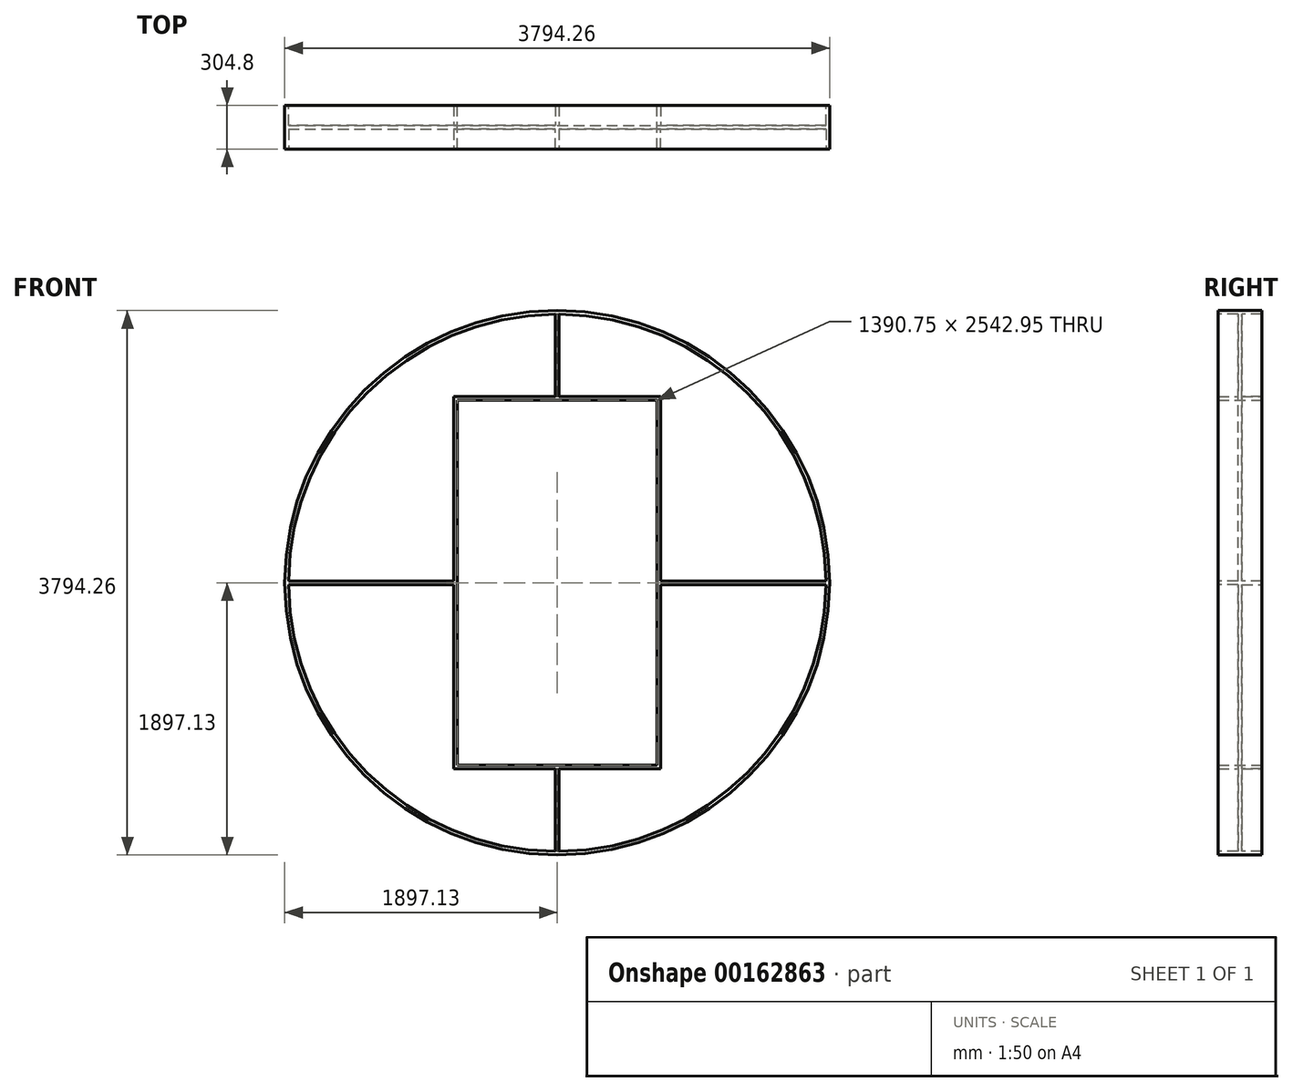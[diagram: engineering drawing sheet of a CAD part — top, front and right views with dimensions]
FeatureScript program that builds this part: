
annotation { "Feature Type Name" : "Feature", "Feature Type Description" : "" }
export const myFeature = defineFeature(function(context is Context, id is Id, definition is map)
    precondition{}
    {
        {
            var Q0;
            Q0=qCreatedBy(makeId("Front.planeOp"),FACE);
            var sketch = newSketch(context, id + "F0", { "sketchPlane" : qUnion([Q0])});
            skCircle(sketch, "E0", {"center": v(0, 0) * mm, "radius": 1897.13 * mm});
            skLineSegment(sketch, "E1.bottom", {"start": v(695.38, -1271.47) * mm, "end": v(-695.38, -1271.47) * mm});
            skLineSegment(sketch, "E1.top", {"start": v(695.38, 1271.47) * mm, "end": v(-695.38, 1271.47) * mm});
            skLineSegment(sketch, "E1.left", {"start": v(695.38, -1271.47) * mm, "end": v(695.38, 1271.47) * mm});
            skLineSegment(sketch, "E1.right", {"start": v(-695.38, -1271.47) * mm, "end": v(-695.38, 1271.47) * mm});
            skPoint(sketch, "E2.orphan", {"position": v(0, 1897.13) * mm});
            skSolve(sketch);
        }
        {
            var Q0;
            Q0 = qSketchRegion(id + "F0", true);
            extrude(context, id + "F1", {"entities" : qUnion([Q0]), "depth" : 304.8 * mm});
        }
        {
            var Q0;
            Q0=makeQuery(id+"F1.opExtrude","CAP_FACE",FACE,{"disambiguationData":[OSD([sQuery(id+"F0.wireOp",EDGE,"E0"),sQuery(id+"F0.wireOp",EDGE,"E1.bottom"),sQuery(id+"F0.wireOp",EDGE,"E1.top"),sQuery(id+"F0.wireOp",EDGE,"E1.left"),sQuery(id+"F0.wireOp",EDGE,"E1.right")])],"isStart":false});
            var sketch = newSketch(context, id + "F2", { "sketchPlane" : qUnion([Q0])});
            skCircle(sketch, "E3", {"center": v(0, 0) * mm, "radius": 1871.73 * mm});
            skLineSegment(sketch, "E4.bottom", {"start": v(720.78, -1296.87) * mm, "end": v(-720.78, -1296.87) * mm});
            skLineSegment(sketch, "E4.top", {"start": v(720.78, 1296.87) * mm, "end": v(-720.78, 1296.87) * mm});
            skLineSegment(sketch, "E4.left", {"start": v(720.78, -1296.87) * mm, "end": v(720.78, 1296.87) * mm});
            skLineSegment(sketch, "E4.right", {"start": v(-720.78, -1296.87) * mm, "end": v(-720.78, 1296.87) * mm});
            skSolve(sketch);
        }
        {
            var Q0;
            Q0 = qSketchRegion(id + "F2", true);
            extrude(context, id + "F3", {"entities" : qUnion([Q0]), "operationType" : NewBodyOperationType.REMOVE, "oppositeDirection" : true, "depth" : 139.7 * mm});
        }
        {
            var Q0;
            Q0=makeQuery(id+"F1.opExtrude","CAP_FACE",FACE,{"disambiguationData":[OSD([sQuery(id+"F0.wireOp",EDGE,"E0"),sQuery(id+"F0.wireOp",EDGE,"E1.bottom"),sQuery(id+"F0.wireOp",EDGE,"E1.top"),sQuery(id+"F0.wireOp",EDGE,"E1.left"),sQuery(id+"F0.wireOp",EDGE,"E1.right")])],"isStart":true});
            var sketch = newSketch(context, id + "F4", { "sketchPlane" : qUnion([Q0])});
            skCircle(sketch, "E5", {"center": v(0, 0) * mm, "radius": 1871.73 * mm});
            skLineSegment(sketch, "E6.bottom", {"start": v(720.78, -1296.87) * mm, "end": v(-720.78, -1296.87) * mm});
            skLineSegment(sketch, "E6.top", {"start": v(720.78, 1296.87) * mm, "end": v(-720.78, 1296.87) * mm});
            skLineSegment(sketch, "E6.left", {"start": v(720.78, -1296.87) * mm, "end": v(720.78, 1296.87) * mm});
            skLineSegment(sketch, "E6.right", {"start": v(-720.78, -1296.87) * mm, "end": v(-720.78, 1296.87) * mm});
            skSolve(sketch);
        }
        {
            var Q0;
            Q0 = qSketchRegion(id + "F4", true);
            extrude(context, id + "F5", {"entities" : qUnion([Q0]), "operationType" : NewBodyOperationType.REMOVE, "oppositeDirection" : true, "depth" : 139.7 * mm});
        }
        {
            var Q0;
            Q0=makeQuery(id+"F3.boolean.opBoolean","COPY",FACE,{"derivedFrom":makeQuery(id+"F3.opExtrude","SWEPT_FACE",FACE,{"disambiguationData":[OSD([sQuery(id+"F2.wireOp",EDGE,"E4.left")])]})});
            var sketch = newSketch(context, id + "F6", { "sketchPlane" : qUnion([Q0])});
            skLineSegment(sketch, "E7.bottom", {"start": v(-304.8, 12.7) * mm, "end": v(-165.1, 12.7) * mm});
            skLineSegment(sketch, "E7.top", {"start": v(-304.8, -12.7) * mm, "end": v(-165.1, -12.7) * mm});
            skLineSegment(sketch, "E7.left", {"start": v(-304.8, 12.7) * mm, "end": v(-304.8, -12.7) * mm});
            skPoint(sketch, "E7.middle", {"position": v(-165.1, 0) * mm});
            skLineSegment(sketch, "E8", {"start": v(-165.1, -12.7) * mm, "end": v(-165.1, 12.7) * mm});
            skPoint(sketch, "E7.right.end.orphan", {"position": v(-25.4, -12.7) * mm});
            skPoint(sketch, "E7.right.start.orphan", {"position": v(-25.4, 12.7) * mm});
            skSolve(sketch);
        }
        {
            var Q0;
            Q0 = qSketchRegion(id + "F6", true);
            var Q1;
            Q1=makeQuery(id+"F3.boolean.opBoolean","COPY",FACE,{"derivedFrom":makeQuery(id+"F3.opExtrude","SWEPT_FACE",FACE,{"disambiguationData":[OSD([sQuery(id+"F2.wireOp",EDGE,"E3")])]})});
            extrude(context, id + "F7", {"entities" : qUnion([Q0]), "endBound" : BoundingType.UP_TO_SURFACE, "endBoundEntityFace" : qUnion([Q1]), "depth" : 25.4 * mm});
        }
        {
            var Q0;
            Q0=makeQuery(id+"F7.opExtrude","SWEPT_BODY",BODY,{"disambiguationData":[OSD([sQuery(id+"F6.wireOp",EDGE,"E7.bottom"),sQuery(id+"F6.wireOp",EDGE,"E7.top"),sQuery(id+"F6.wireOp",EDGE,"E7.left"),sQuery(id+"F6.wireOp",EDGE,"E8")])]});
            var Q1;
            Q1=qCreatedBy(makeId("Right.planeOp"),FACE);
            mirror(context, id + "F8", {"operationType" : NewBodyOperationType.ADD, "entities" : qUnion([Q0]), "mirrorPlane" : qUnion([Q1])});
        }
        {
            var Q0;
            Q0=makeQuery(id+"F3.boolean.opBoolean","COPY",FACE,{"derivedFrom":makeQuery(id+"F3.opExtrude","SWEPT_FACE",FACE,{"disambiguationData":[OSD([sQuery(id+"F2.wireOp",EDGE,"E4.top")])]})});
            var sketch = newSketch(context, id + "F9", { "sketchPlane" : qUnion([Q0])});
            skLineSegment(sketch, "E9.bottom", {"start": v(-12.7, -304.8) * mm, "end": v(12.7, -304.8) * mm});
            skLineSegment(sketch, "E9.left", {"start": v(-12.7, -304.8) * mm, "end": v(-12.7, -165.1) * mm});
            skLineSegment(sketch, "E9.right", {"start": v(12.7, -304.8) * mm, "end": v(12.7, -165.1) * mm});
            skPoint(sketch, "E9.middle", {"position": v(0, -165.1) * mm});
            skLineSegment(sketch, "E10", {"start": v(12.7, -165.1) * mm, "end": v(-12.7, -165.1) * mm});
            skPoint(sketch, "E9.top.end.orphan", {"position": v(12.7, -25.4) * mm});
            skPoint(sketch, "E9.top.start.orphan", {"position": v(-12.7, -25.4) * mm});
            skSolve(sketch);
        }
        {
            var Q0;
            Q0 = qSketchRegion(id + "F9", true);
            var Q1;
            {var subQ1=sQuery(id+"F2.wireOp",EDGE,"E3");var subQ2=makeQuery(id+"F7.opExtrude","SWEPT_FACE",FACE,{"disambiguationData":[OSD([sQuery(id+"F6.wireOp",EDGE,"E7.bottom")])]});Q1=makeQuery(id+"F8.boolean.opBoolean","SPLIT",FACE,{"disambiguationData":[TD([subQ2])],"derivedFrom":makeQuery(id+"F3.boolean.opBoolean","COPY",FACE,{"derivedFrom":makeQuery(id+"F3.opExtrude","SWEPT_FACE",FACE,{"disambiguationData":[OSD([subQ1])]})})});}
            extrude(context, id + "F10", {"entities" : qUnion([Q0]), "endBound" : BoundingType.UP_TO_SURFACE, "endBoundEntityFace" : qUnion([Q1]), "depth" : 25.4 * mm});
        }
        {
            var Q0;
            Q0=makeQuery(id+"F10.opExtrude","SWEPT_BODY",BODY,{"disambiguationData":[OSD([sQuery(id+"F9.wireOp",EDGE,"E9.bottom"),sQuery(id+"F9.wireOp",EDGE,"E9.left"),sQuery(id+"F9.wireOp",EDGE,"E9.right"),sQuery(id+"F9.wireOp",EDGE,"E10")])]});
            var Q1;
            Q1=qCreatedBy(makeId("Top.planeOp"),FACE);
            mirror(context, id + "F11", {"operationType" : NewBodyOperationType.ADD, "entities" : qUnion([Q0]), "mirrorPlane" : qUnion([Q1])});
        }
        {
            var Q0;
            Q0=makeQuery(id+"F5.boolean.opBoolean","COPY",FACE,{"derivedFrom":makeQuery(id+"F5.opExtrude","SWEPT_FACE",FACE,{"disambiguationData":[OSD([sQuery(id+"F4.wireOp",EDGE,"E6.top")])]})});
            var sketch = newSketch(context, id + "F12", { "sketchPlane" : qUnion([Q0])});
            skLineSegment(sketch, "E11.bottom", {"start": v(12.58, 0) * mm, "end": v(-12.82, -0.16) * mm});
            skLineSegment(sketch, "E11.left", {"start": v(12.58, 0) * mm, "end": v(12.7, -139.62) * mm});
            skLineSegment(sketch, "E11.right", {"start": v(-12.82, -0.16) * mm, "end": v(-12.7, -139.78) * mm});
            skPoint(sketch, "E11.middle", {"position": v(0, -139.7) * mm});
            skLineSegment(sketch, "E12", {"start": v(-12.7, -139.78) * mm, "end": v(12.7, -139.62) * mm});
            skPoint(sketch, "E11.top.end.orphan", {"position": v(-12.58, -279.4) * mm});
            skPoint(sketch, "E13.orphan", {"position": v(12.82, -279.24) * mm});
            skSolve(sketch);
        }
        {
            var Q0;
            Q0 = qSketchRegion(id + "F12", true);
            var Q1;
            Q1=makeQuery(id+"F5.boolean.opBoolean","COPY",FACE,{"derivedFrom":makeQuery(id+"F5.opExtrude","SWEPT_FACE",FACE,{"disambiguationData":[OSD([sQuery(id+"F4.wireOp",EDGE,"E5")])]})});
            extrude(context, id + "F13", {"entities" : qUnion([Q0]), "endBound" : BoundingType.UP_TO_SURFACE, "endBoundEntityFace" : qUnion([Q1]), "depth" : 25.4 * mm});
        }
        {
            var Q0;
            Q0=makeQuery(id+"F13.opExtrude","SWEPT_BODY",BODY,{"disambiguationData":[OSD([sQuery(id+"F12.wireOp",EDGE,"E11.bottom"),sQuery(id+"F12.wireOp",EDGE,"E11.left"),sQuery(id+"F12.wireOp",EDGE,"E11.right"),sQuery(id+"F12.wireOp",EDGE,"E12")])]});
            var Q1;
            Q1=qCreatedBy(makeId("Top.planeOp"),FACE);
            mirror(context, id + "F14", {"operationType" : NewBodyOperationType.ADD, "entities" : qUnion([Q0]), "mirrorPlane" : qUnion([Q1])});
        }
        {
            var Q0;
            Q0=makeQuery(id+"F5.boolean.opBoolean","COPY",FACE,{"derivedFrom":makeQuery(id+"F5.opExtrude","SWEPT_FACE",FACE,{"disambiguationData":[OSD([sQuery(id+"F4.wireOp",EDGE,"E6.left")])]})});
            var sketch = newSketch(context, id + "F15", { "sketchPlane" : qUnion([Q0])});
            skLineSegment(sketch, "E14.bottom", {"start": v(0, -12.7) * mm, "end": v(139.7, -12.7) * mm});
            skLineSegment(sketch, "E14.top", {"start": v(0, 12.7) * mm, "end": v(139.7, 12.7) * mm});
            skLineSegment(sketch, "E14.left", {"start": v(0, -12.7) * mm, "end": v(0, 12.7) * mm});
            skPoint(sketch, "E14.middle", {"position": v(139.7, 0) * mm});
            skLineSegment(sketch, "E15", {"start": v(139.7, -12.7) * mm, "end": v(139.7, 12.7) * mm});
            skPoint(sketch, "E14.right.end.orphan", {"position": v(279.4, 12.7) * mm});
            skPoint(sketch, "E14.right.start.orphan", {"position": v(279.4, -12.7) * mm});
            skSolve(sketch);
        }
        {
            var Q0;
            Q0 = qSketchRegion(id + "F15", true);
            var Q1;
            {var subQ1=sQuery(id+"F4.wireOp",EDGE,"E5");var subQ2=makeQuery(id+"F13.opExtrude","SWEPT_FACE",FACE,{"disambiguationData":[OSD([sQuery(id+"F12.wireOp",EDGE,"E11.right")])]});var subQ3=makeQuery(id+"F5.boolean.opBoolean","COPY",FACE,{"derivedFrom":makeQuery(id+"F5.opExtrude","SWEPT_FACE",FACE,{"disambiguationData":[OSD([subQ1])]})});Q1=makeQuery(id+"F14.boolean.opBoolean","SPLIT",FACE,{"disambiguationData":[TD([subQ2])],"derivedFrom":subQ3});}
            extrude(context, id + "F16", {"entities" : qUnion([Q0]), "endBound" : BoundingType.UP_TO_SURFACE, "endBoundEntityFace" : qUnion([Q1]), "depth" : 25.4 * mm});
        }
        {
            var Q0;
            Q0=makeQuery(id+"F16.opExtrude","SWEPT_BODY",BODY,{"disambiguationData":[OSD([sQuery(id+"F15.wireOp",EDGE,"E14.bottom"),sQuery(id+"F15.wireOp",EDGE,"E14.top"),sQuery(id+"F15.wireOp",EDGE,"E14.left"),sQuery(id+"F15.wireOp",EDGE,"E15")])]});
            var Q1;
            Q1=qCreatedBy(makeId("Right.planeOp"),FACE);
            mirror(context, id + "F17", {"operationType" : NewBodyOperationType.ADD, "entities" : qUnion([Q0]), "mirrorPlane" : qUnion([Q1])});
        }
    });
